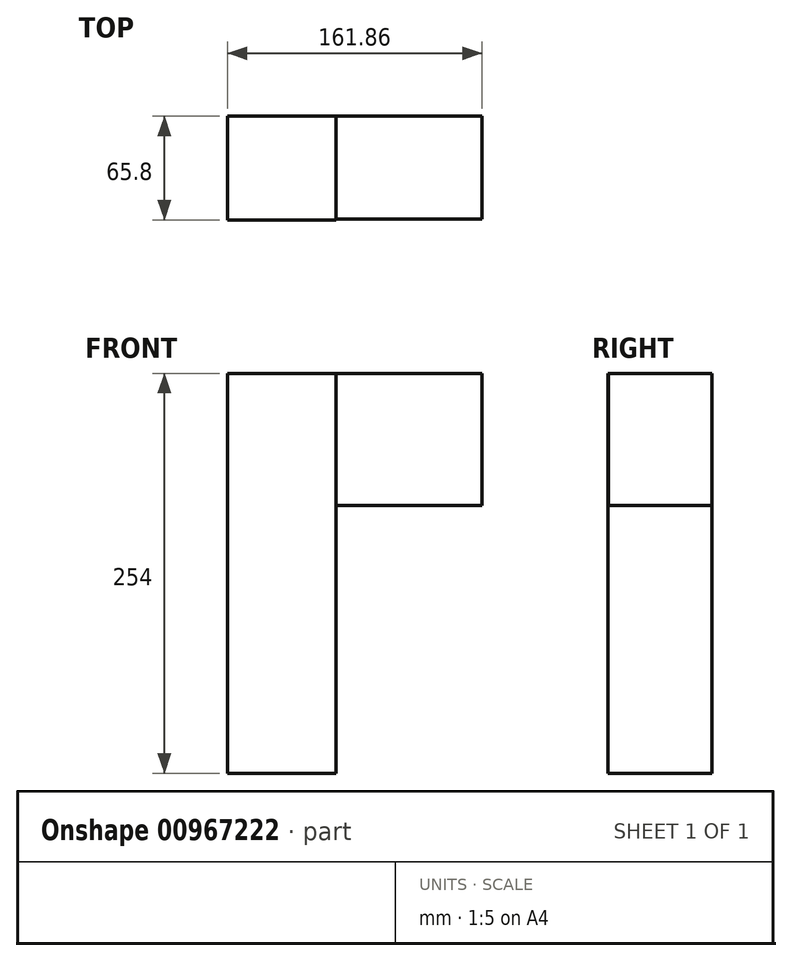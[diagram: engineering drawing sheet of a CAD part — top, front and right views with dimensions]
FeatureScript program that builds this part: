
annotation { "Feature Type Name" : "Feature", "Feature Type Description" : "" }
export const myFeature = defineFeature(function(context is Context, id is Id, definition is map)
    precondition{}
    {
        {
            var Q0;
            Q0=qCreatedBy(makeId("Top.planeOp"),FACE);
            var sketch = newSketch(context, id + "F0", { "sketchPlane" : qUnion([Q0])});
            skLineSegment(sketch, "E0.bottom", {"start": v(68.91, -65.8) * mm, "end": v(0, -65.8) * mm});
            skLineSegment(sketch, "E0.top", {"start": v(68.91, 0) * mm, "end": v(0, 0) * mm});
            skLineSegment(sketch, "E0.left", {"start": v(68.91, -65.8) * mm, "end": v(68.91, 0) * mm});
            skLineSegment(sketch, "E0.right", {"start": v(0, -65.8) * mm, "end": v(0, 0) * mm});
            skSolve(sketch);
        }
        {
            var Q0;
            Q0=makeQuery(id+"F0.imprint","IMPRINT",FACE,{"disambiguationData":[TD([[makeQuery(id+"F0.imprint","IMPRINT",EDGE,{"derivedFrom":sQuery(id+"F0.wireOp",EDGE,"E0.bottom")}),-1.0]])]});
            extrude(context, id + "F1", {"entities" : qUnion([Q0]), "depth" : 254 * mm, "offsetDistance" : 25.4 * mm});
        }
        {
            var Q0;
            Q0=makeQuery(id+"F1.opExtrude","SWEPT_FACE",FACE,{"disambiguationData":[OSD([sQuery(id+"F0.wireOp",EDGE,"E0.left")])]});
            var sketch = newSketch(context, id + "F2", { "sketchPlane" : qUnion([Q0])});
            skLineSegment(sketch, "E1.bottom", {"start": v(0, 254) * mm, "end": v(-65.8, 254) * mm});
            skLineSegment(sketch, "E1.top", {"start": v(0, 165.84) * mm, "end": v(-65.8, 165.84) * mm});
            skLineSegment(sketch, "E1.left", {"start": v(0, 254) * mm, "end": v(0, 165.84) * mm});
            skLineSegment(sketch, "E1.right", {"start": v(-65.8, 254) * mm, "end": v(-65.8, 165.84) * mm});
            skSolve(sketch);
        }
        {
            var Q0;
            Q0=makeQuery(id+"F2.imprint","IMPRINT",FACE,{"disambiguationData":[TD([[makeQuery(id+"F2.imprint","IMPRINT",EDGE,{"derivedFrom":sQuery(id+"F2.wireOp",EDGE,"E1.bottom")}),-1.0]])]});
            var sketch = newSketch(context, id + "F3", { "sketchPlane" : qUnion([Q0])});
            skLineSegment(sketch, "E2.bottom", {"start": v(0, 253.83) * mm, "end": v(-65.43, 253.83) * mm});
            skLineSegment(sketch, "E2.top", {"start": v(0, 170.02) * mm, "end": v(-65.43, 170.02) * mm});
            skLineSegment(sketch, "E2.left", {"start": v(-65.43, 253.83) * mm, "end": v(-65.43, 170.02) * mm});
            skLineSegment(sketch, "E2.right", {"start": v(0, 253.83) * mm, "end": v(0, 170.02) * mm});
            skSolve(sketch);
        }
        {
            var Q0;
            Q0=makeQuery(id+"F3.imprint","IMPRINT",FACE,{"disambiguationData":[TD([[makeQuery(id+"F3.imprint","IMPRINT",EDGE,{"derivedFrom":sQuery(id+"F3.wireOp",EDGE,"E2.bottom")}),1.0]])]});
            var Q1;
            Q1 = qSketchRegion(id + "F3", true);
            extrude(context, id + "F4", {"entities" : qUnion([Q0, Q1]), "operationType" : NewBodyOperationType.ADD, "depth" : 92.95 * mm, "offsetDistance" : 25.4 * mm});
        }
    });
